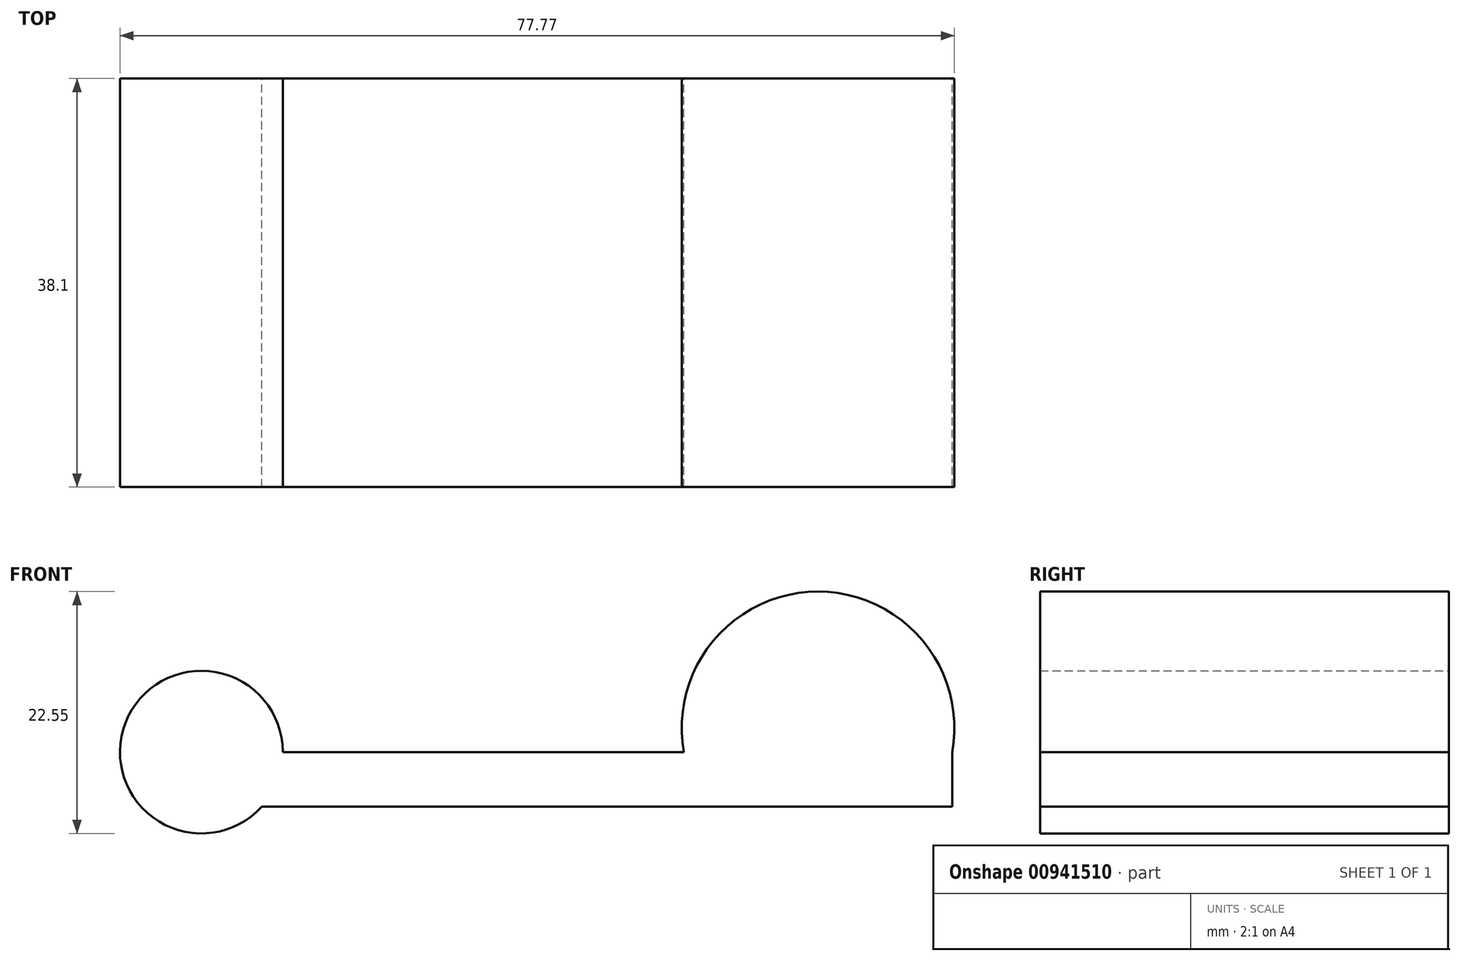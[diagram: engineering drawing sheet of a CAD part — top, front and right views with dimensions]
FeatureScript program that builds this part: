
annotation { "Feature Type Name" : "Feature", "Feature Type Description" : "" }
export const myFeature = defineFeature(function(context is Context, id is Id, definition is map)
    precondition{}
    {
        {
            var Q0;
            Q0=qCreatedBy(makeId("Front.planeOp"),FACE);
            var sketch = newSketch(context, id + "F0", { "sketchPlane" : qUnion([Q0])});
            skArc(sketch, "E0", {"start": v(12.5, -2.27) * mm, "mid": v(0, 12.7) * mm, "end": v(-12.5, -2.27) * mm});
            skLineSegment(sketch, "E1", {"start": v(-57.48, -2.27) * mm, "end": v(12.5, -2.27) * mm});
            skLineSegment(sketch, "E2", {"start": v(-57.48, -2.27) * mm, "end": v(-57.48, -7.35) * mm});
            skLineSegment(sketch, "E3", {"start": v(-57.48, -7.35) * mm, "end": v(12.5, -7.35) * mm});
            skLineSegment(sketch, "E4", {"start": v(12.5, -7.35) * mm, "end": v(12.5, -2.27) * mm});
            skCircle(sketch, "E5", {"center": v(-57.48, -2.27) * mm, "radius": 7.59 * mm});
            skSolve(sketch);
        }
        {
            var Q0;
            Q0 = qSketchRegion(id + "F0", true);
            extrude(context, id + "F1", {"entities" : qUnion([Q0]), "depth" : 38.1 * mm, "offsetDistance" : 25.4 * mm});
        }
        {
            var Q0;
            Q0=qCreatedBy(makeId("Front.planeOp"),FACE);
            var sketch = newSketch(context, id + "F2", { "sketchPlane" : qUnion([Q0])});
            skArc(sketch, "E6", {"start": v(-37.69, -2.43) * mm, "mid": v(-47.77, 5.89) * mm, "end": v(-60.78, 4.59) * mm});
            skSolve(sketch);
        }
        {
            var Q0;
            Q0=sQuery(id+"F2.wireOp",EDGE,"E6");
            extrude(context, id + "F3", {"bodyType" : ToolBodyType.SURFACE, "surfaceEntities" : qUnion([Q0]), "depth" : 25.4 * mm, "offsetDistance" : 25.4 * mm});
        }
    });
